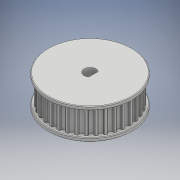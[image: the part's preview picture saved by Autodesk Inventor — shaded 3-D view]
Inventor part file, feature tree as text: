
AUTODESK INVENTOR PART (.ipt)
format: ipt  version: 2018 (Build 220112000, 112)  size: 451,584 bytes
history: native  units: mm
features: extrude x5, sketch x4, other x1, pattern_circular x1, fillet x1
ambient origin geometry x8: Origin, YZ Plane, XZ Plane, XY Plane, X Axis, Y Axis, Z Axis, Center Point
bodies: Solid1 (feature_tree)
feature tree (12):
  other  "Tooth"
  extrude  "Gear Solid Extrusion"  Depth=1.5mm
  extrude  "Tooth Cut-Out Extrusion"  Depth=0.85mm
  pattern_circular  "Teeth Array"  [2 undecoded]
  extrude  "Flange Extrusion Front"  TaperAngle=0.0deg  [1 undecoded]
  extrude  "Flange Extrusion Back"  Depth=10.0mm TaperAngle=0.0deg
  fillet  "Flange Fillet"  Radius=350.0mm
  extrude  "Extrusion5"  TaperAngle=360.0deg  [1 undecoded]
  sketch  "Sketch2"  dims[d2=16.711269mm d3=1.5mm]
  sketch  "Sketch3"  dims[d4=1.14mm d5=0.85mm]
  sketch  "Sketch4"  dims[d6=0.61mm]
  sketch  "Sketch5"  dims[d7=0.25mm d8=2.0mm d11=0.0mm d12=10.0mm d13=0.0mm d14=350.0mm d15=360.0deg d17=17.711269mm d19=0.0mm d20=17.711269mm d21=1.5mm d22=0.0mm d23=0.25mm d24=2.5mm d25=1.5mm d26=10.0mm d27=0.0mm]
note: 4 required parameter values undecoded (feature->parameter linkage not recoverable at this tier; creation-order binding heuristic only, values carry confidence <= 0.55)
